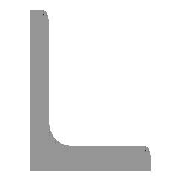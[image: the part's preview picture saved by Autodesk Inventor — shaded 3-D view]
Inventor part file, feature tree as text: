
AUTODESK INVENTOR PART (.ipt)
format: ipt  version: 2016 (Build 200138000, 138)  size: 124,416 bytes
history: native  units: mm (DEFAULTED — no unit token found)
features: other x4, sketch x3, plane x2, extrude x1
ambient origin geometry x8: Origin, YZ Plane, XZ Plane, XY Plane, X Axis, Y Axis, Z Axis, Center Point
bodies: Solid1 (feature_tree)
feature tree (10):
  parser-record x1  (decoder bookkeeping rows leaked as tree rows — omitted from the tree; the rows remain in map.json)
  other  "Driven Length"
  other  "Plano inicial"
  other  "Plano final"
  extrude  "Cuerpo"  Depth=38.1mm
  sketch  "Boceto5"  dims[d3=4.7625mm d4=2400.0mm d5=0.0mm d10=0.0mm d11=0.0mm d12=-0.0mm d13=2400.0mm d14=4.826mm d15=2.286mm d16=90.0deg d17=2400.0mm]
  plane  "Plano de trabajo4"
  sketch  "Sketch3"  dims[d0=38.1mm d1=38.1mm]
  plane  "Work Plane3"
  sketch  "Sketch4"  dims[d2=4.7625mm]
